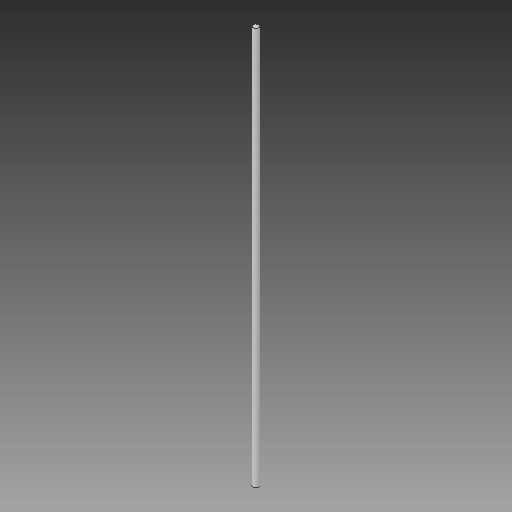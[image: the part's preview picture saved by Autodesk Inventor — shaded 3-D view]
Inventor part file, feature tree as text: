
AUTODESK INVENTOR PART (.ipt)
format: ipt  version: 2017 (Build 210142000, 142)  size: 69,632 bytes
history: native  units: mm
features: extrude x1, sketch x1
ambient origin geometry x8: Origin, YZ Plane, XZ Plane, XY Plane, X Axis, Y Axis, Z Axis, Center Point
bodies: Solid1 (feature_tree)
feature tree (2):
  extrude  "Extrusion1"  Depth=830.0mm TaperAngle=0.0deg
  sketch  "Sketch1"  dims[d0=12.0mm d1=830.0mm d2=0.0mm]
